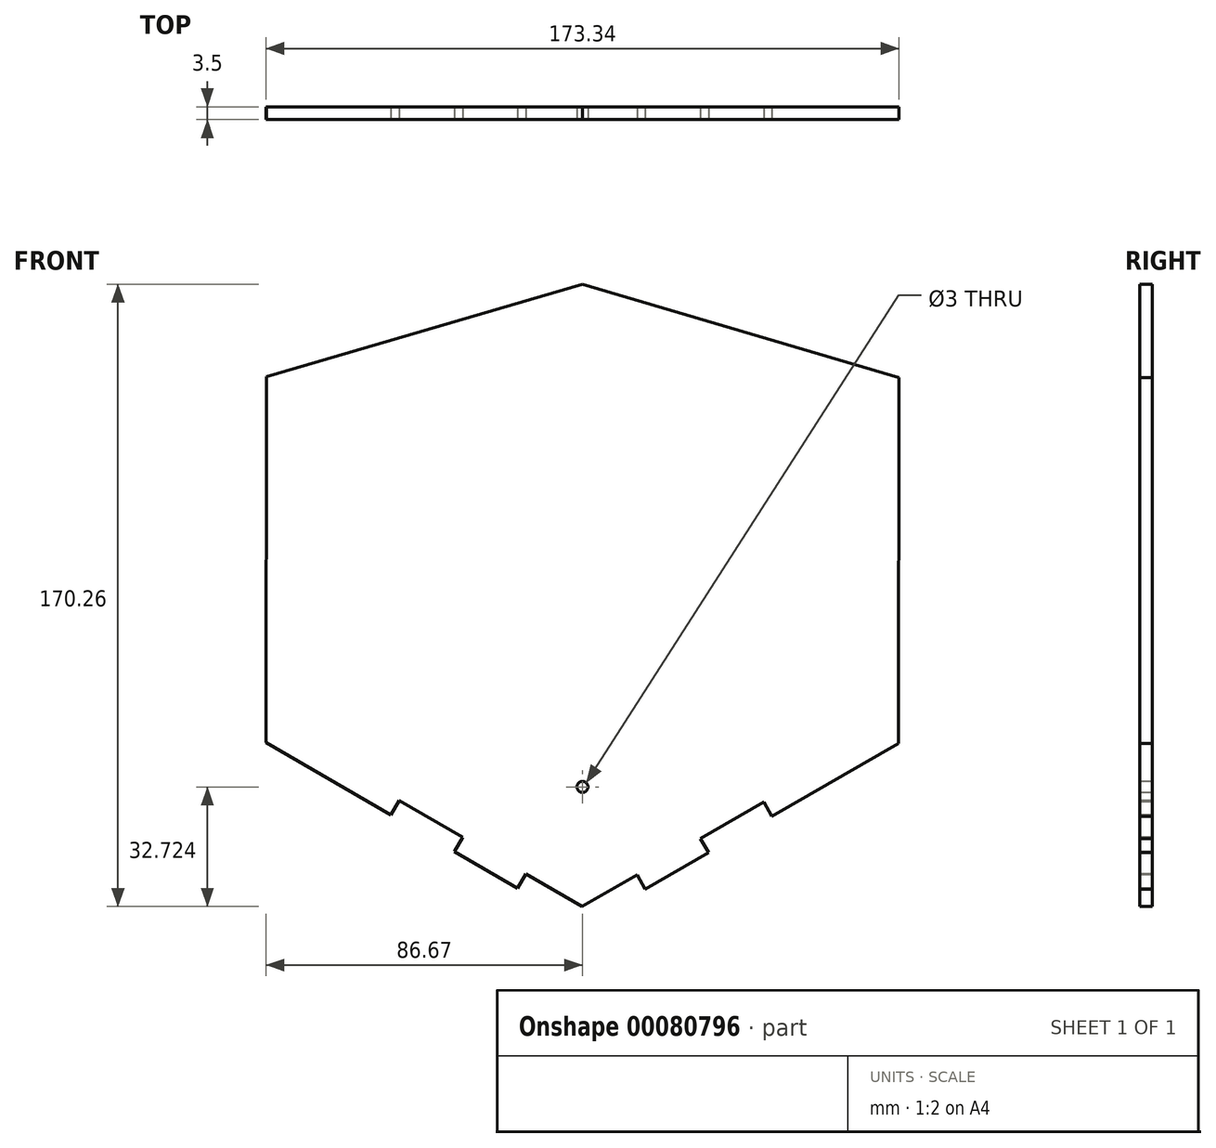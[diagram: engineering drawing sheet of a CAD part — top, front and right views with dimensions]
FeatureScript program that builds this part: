
annotation { "Feature Type Name" : "Feature", "Feature Type Description" : "" }
export const myFeature = defineFeature(function(context is Context, id is Id, definition is map)
    precondition{}
    {
        {
            var Q0;
            Q0=qCreatedBy(makeId("Front.planeOp"),FACE);
            var sketch = newSketch(context, id + "F0", { "sketchPlane" : qUnion([Q0])});
            skCircle(sketch, "E0.cCircle", {"center": v(0, 0) * mm, "radius": 86.6 * mm, "construction": true});
            skLineSegment(sketch, "E0.0", {"start": v(-86.54, 50.12) * mm, "end": v(0.13, 100) * mm});
            skLineSegment(sketch, "E0.1", {"start": v(0.13, 100) * mm, "end": v(86.67, 49.88) * mm});
            skLineSegment(sketch, "E0.2", {"start": v(86.67, 49.88) * mm, "end": v(86.54, -50.12) * mm});
            skLineSegment(sketch, "E0.3", {"start": v(86.54, -50.12) * mm, "end": v(-0.13, -100) * mm});
            skLineSegment(sketch, "E0.4", {"start": v(-0.13, -100) * mm, "end": v(-86.67, -49.88) * mm});
            skLineSegment(sketch, "E0.5", {"start": v(-86.67, -49.88) * mm, "end": v(-86.54, 50.12) * mm});
            skPoint(sketch, "E0.0.midPoint", {"position": v(-43.2, 75.06) * mm});
            skLineSegment(sketch, "E1", {"start": v(-86.54, 50.12) * mm, "end": v(0, 75.46) * mm});
            skLineSegment(sketch, "E2", {"start": v(0, 75.46) * mm, "end": v(86.67, 49.88) * mm});
            skSolve(sketch);
        }
        {
            var Q0;
            Q0=makeQuery(id+"F0.imprint","IMPRINT",FACE,{"disambiguationData":[TD([[makeQuery(id+"F0.imprint","IMPRINT",EDGE,{"derivedFrom":sQuery(id+"F0.wireOp",EDGE,"E0.2")}),-1.0]])]});
            extrude(context, id + "F1", {"entities" : qUnion([Q0]), "depth" : 3.5 * mm});
        }
        {
            var Q0;
            Q0=makeQuery(id+"F1.opExtrude","CAP_FACE",FACE,{"disambiguationData":[OSD([sQuery(id+"F0.wireOp",EDGE,"E0.0"),sQuery(id+"F0.wireOp",EDGE,"E0.1"),sQuery(id+"F0.wireOp",EDGE,"E0.2"),sQuery(id+"F0.wireOp",EDGE,"E0.3"),sQuery(id+"F0.wireOp",EDGE,"E0.4"),sQuery(id+"F0.wireOp",EDGE,"E0.5")])],"isStart":false});
            var sketch = newSketch(context, id + "F2", { "sketchPlane" : qUnion([Q0])});
            skLineSegment(sketch, "E3", {"start": v(-66.96, 56.2) * mm, "end": v(-69.2, 60.1) * mm});
            skLineSegment(sketch, "E4", {"start": v(-69.2, 60.1) * mm, "end": v(-51.87, 70.07) * mm});
            skLineSegment(sketch, "E5", {"start": v(-51.87, 70.07) * mm, "end": v(-49.62, 66.17) * mm});
            skLineSegment(sketch, "E6", {"start": v(-49.62, 66.17) * mm, "end": v(-32.29, 76.15) * mm});
            skLineSegment(sketch, "E7", {"start": v(-32.29, 76.15) * mm, "end": v(-34.53, 80.05) * mm});
            skLineSegment(sketch, "E8", {"start": v(-34.53, 80.05) * mm, "end": v(-17.2, 90.02) * mm});
            skLineSegment(sketch, "E9", {"start": v(-17.2, 90.02) * mm, "end": v(-17.2, 90.02) * mm});
            skLineSegment(sketch, "E10", {"start": v(-17.2, 90.02) * mm, "end": v(0.13, 100) * mm});
            skLineSegment(sketch, "E11", {"start": v(0.13, 100) * mm, "end": v(2.38, 96.1) * mm});
            skLineSegment(sketch, "E12", {"start": v(-17.2, 90.02) * mm, "end": v(-14.95, 86.12) * mm});
            skLineSegment(sketch, "E13", {"start": v(-14.95, 86.12) * mm, "end": v(2.38, 96.1) * mm});
            skLineSegment(sketch, "E14", {"start": v(-86.67, -49.88) * mm, "end": v(-82.14, -49.89) * mm});
            skLineSegment(sketch, "E15", {"start": v(-86.67, -49.88) * mm, "end": v(-86.67, -49.88) * mm});
            skLineSegment(sketch, "E16", {"start": v(-86.54, 50.11) * mm, "end": v(-86.54, 50.12) * mm});
            skLineSegment(sketch, "E17", {"start": v(86.54, -50.12) * mm, "end": v(82.06, -50.11) * mm});
            skLineSegment(sketch, "E18", {"start": v(86.67, 49.88) * mm, "end": v(86.67, 49.89) * mm});
            skLineSegment(sketch, "E19", {"start": v(86.54, -50.12) * mm, "end": v(86.54, -50.12) * mm});
            skLineSegment(sketch, "E20", {"start": v(43.43, 74.93) * mm, "end": v(0.13, 100) * mm});
            skLineSegment(sketch, "E21", {"start": v(67.1, 56.01) * mm, "end": v(69.36, 59.9) * mm});
            skLineSegment(sketch, "E22", {"start": v(69.36, 59.9) * mm, "end": v(52.05, 69.93) * mm});
            skLineSegment(sketch, "E23", {"start": v(52.05, 69.93) * mm, "end": v(49.8, 66.04) * mm});
            skLineSegment(sketch, "E24", {"start": v(49.8, 66.04) * mm, "end": v(32.5, 76.06) * mm});
            skLineSegment(sketch, "E25", {"start": v(32.5, 76.06) * mm, "end": v(34.75, 79.95) * mm});
            skLineSegment(sketch, "E26", {"start": v(34.75, 79.95) * mm, "end": v(17.44, 89.98) * mm});
            skLineSegment(sketch, "E27", {"start": v(17.44, 89.98) * mm, "end": v(15.18, 86.08) * mm});
            skLineSegment(sketch, "E28", {"start": v(15.18, 86.08) * mm, "end": v(-2.12, 96.1) * mm});
            skLineSegment(sketch, "E29", {"start": v(-2.12, 96.1) * mm, "end": v(0.13, 100) * mm});
            skLineSegment(sketch, "E30", {"start": v(-86.67, -49.88) * mm, "end": v(-84.41, -45.99) * mm});
            skLineSegment(sketch, "E31", {"start": v(-84.41, -45.99) * mm, "end": v(-67.1, -56.01) * mm});
            skLineSegment(sketch, "E32", {"start": v(-67.1, -56.01) * mm, "end": v(-69.7, -59.7) * mm});
            skLineSegment(sketch, "E33", {"start": v(-69.7, -59.7) * mm, "end": v(-52.4, -69.73) * mm});
            skLineSegment(sketch, "E34", {"start": v(-52.4, -69.73) * mm, "end": v(-50.13, -65.83) * mm});
            skLineSegment(sketch, "E35", {"start": v(-50.13, -65.83) * mm, "end": v(-32.83, -75.86) * mm});
            skLineSegment(sketch, "E36", {"start": v(-32.83, -75.86) * mm, "end": v(-35.09, -79.76) * mm});
            skLineSegment(sketch, "E37", {"start": v(-35.09, -79.76) * mm, "end": v(-17.78, -89.78) * mm});
            skLineSegment(sketch, "E38", {"start": v(-17.78, -89.78) * mm, "end": v(-15.52, -85.89) * mm});
            skLineSegment(sketch, "E39", {"start": v(-15.52, -85.89) * mm, "end": v(1.78, -95.91) * mm});
            skLineSegment(sketch, "E40", {"start": v(1.78, -95.91) * mm, "end": v(-0.47, -99.8) * mm});
            skLineSegment(sketch, "E41", {"start": v(-0.47, -99.8) * mm, "end": v(-0.13, -100) * mm});
            skLineSegment(sketch, "E42", {"start": v(-0.13, -100) * mm, "end": v(-2.38, -96.1) * mm});
            skLineSegment(sketch, "E43", {"start": v(-2.38, -96.1) * mm, "end": v(14.95, -86.12) * mm});
            skLineSegment(sketch, "E44", {"start": v(14.95, -86.12) * mm, "end": v(17.2, -90.02) * mm});
            skLineSegment(sketch, "E45", {"start": v(17.2, -90.02) * mm, "end": v(34.53, -80.05) * mm});
            skLineSegment(sketch, "E46", {"start": v(34.53, -80.05) * mm, "end": v(32.29, -76.15) * mm});
            skLineSegment(sketch, "E47", {"start": v(32.29, -76.15) * mm, "end": v(49.62, -66.17) * mm});
            skLineSegment(sketch, "E48", {"start": v(49.62, -66.17) * mm, "end": v(51.87, -70.07) * mm});
            skLineSegment(sketch, "E49", {"start": v(52.12, -69.93) * mm, "end": v(69.45, -59.95) * mm});
            skLineSegment(sketch, "E50", {"start": v(69.45, -59.95) * mm, "end": v(67.2, -56.05) * mm});
            skLineSegment(sketch, "E51", {"start": v(67.2, -56.05) * mm, "end": v(84.54, -46.07) * mm});
            skLineSegment(sketch, "E52", {"start": v(84.54, -46.07) * mm, "end": v(86.78, -49.97) * mm});
            skCircle(sketch, "E53", {"center": v(0, -62.08) * mm, "radius": 1.5 * mm});
            skSolve(sketch);
        }
        {
            var Q0;
            Q0=makeQuery(id+"F2.imprint","IMPRINT",FACE,{"disambiguationData":[TD([[makeQuery(id+"F2.imprint","IMPRINT",EDGE,{"derivedFrom":sQuery(id+"F2.wireOp",EDGE,"C7dvouTY-Bt3v-uct5-AHeq-p9BstwpN72ip.bottom")}),-1.0]])]});
            var Q1;
            Q1=makeQuery(id+"F2.imprint","IMPRINT",FACE,{"disambiguationData":[TD([[makeQuery(id+"F2.imprint","IMPRINT",EDGE,{"derivedFrom":sQuery(id+"F2.wireOp",EDGE,"167fa7a6-6e49-4368-af60-a64b96dbe5f00.MirrorCS")}),1.0]])]});
            var Q2;
            {var subQ0=sQuery(id+"F2.wireOp",EDGE,"E21");Q2=makeQuery(id+"F2.imprint","IMPRINT",FACE,{"disambiguationData":[TD([[makeQuery(id+"F2.imprint","IMPRINT",EDGE,{"derivedFrom":subQ0}),-1.0]])]});}
            var Q3;
            {var subQ7=sQuery(id+"F2.wireOp",EDGE,"MmeorMg7-Et77-mlVq-baLl-yIuDlze3Zn6h");Q3=makeQuery(id+"F2.imprint","IMPRINT",FACE,{"disambiguationData":[TD([[makeQuery(id+"F2.imprint","IMPRINT",EDGE,{"derivedFrom":subQ7}),-1.0]])]});}
            var Q4;
            {var subQ0=sQuery(id+"F2.wireOp",EDGE,"Vk6HYr1c-dtAy-F9Vo-Em9N-zrXxlWtmeyFl");Q4=makeQuery(id+"F2.imprint","IMPRINT",FACE,{"disambiguationData":[TD([[makeQuery(id+"F2.imprint","IMPRINT",EDGE,{"derivedFrom":subQ0}),-1.0]])]});}
            var Q5;
            {var subQ4=sQuery(id+"F2.wireOp",EDGE,"E17");Q5=makeQuery(id+"F2.imprint","IMPRINT",FACE,{"disambiguationData":[TD([[makeQuery(id+"F2.imprint","IMPRINT",EDGE,{"derivedFrom":subQ4}),1.0]])]});}
            var Q6;
            {var subQ7=sQuery(id+"F2.wireOp",EDGE,"2hepQ55R-wE0u-Nrot-sNKX-UqjB5rhPEbW4");Q6=makeQuery(id+"F2.imprint","IMPRINT",FACE,{"disambiguationData":[TD([[makeQuery(id+"F2.imprint","IMPRINT",EDGE,{"derivedFrom":subQ7}),-1.0]])]});}
            var Q7;
            {var subQ0=sQuery(id+"F2.wireOp",EDGE,"E46");Q7=makeQuery(id+"F2.imprint","IMPRINT",FACE,{"disambiguationData":[TD([[makeQuery(id+"F2.imprint","IMPRINT",EDGE,{"derivedFrom":subQ0}),-1.0]])]});}
            var Q8;
            {var subQ8=sQuery(id+"F2.wireOp",EDGE,"E38");Q8=makeQuery(id+"F2.imprint","IMPRINT",FACE,{"disambiguationData":[TD([[makeQuery(id+"F2.imprint","IMPRINT",EDGE,{"derivedFrom":subQ8}),-1.0]])]});}
            var Q9;
            {var subQ2=sQuery(id+"F2.wireOp",EDGE,"E14");Q9=makeQuery(id+"F2.imprint","IMPRINT",FACE,{"disambiguationData":[TD([[makeQuery(id+"F2.imprint","IMPRINT",EDGE,{"derivedFrom":subQ2}),-1.0]])]});}
            var Q10;
            {var subQ4=sQuery(id+"F2.wireOp",EDGE,"0MOvUSSM-JEJ4-uT5y-fSHd-BTDzLtKJbzvy");Q10=makeQuery(id+"F2.imprint","IMPRINT",FACE,{"disambiguationData":[TD([[makeQuery(id+"F2.imprint","IMPRINT",EDGE,{"derivedFrom":subQ4}),1.0]])]});}
            var Q11;
            {var subQ1=sQuery(id+"F2.wireOp",EDGE,"TpYNR21e-QnRL-vsfI-uHCN-WWDlJ3sKFpeB");Q11=makeQuery(id+"F2.imprint","IMPRINT",FACE,{"disambiguationData":[TD([[makeQuery(id+"F2.imprint","IMPRINT",EDGE,{"derivedFrom":subQ1}),-1.0]])]});}
            var Q12;
            {var subQ0=sQuery(id+"F2.wireOp",EDGE,"UFPksVoi-JG3M-WY3m-71ca-0zyNUTbbqVwQ");Q12=makeQuery(id+"F2.imprint","IMPRINT",FACE,{"disambiguationData":[TD([[makeQuery(id+"F2.imprint","IMPRINT",EDGE,{"derivedFrom":subQ0}),-1.0]])]});}
            var Q13;
            {var subQ5=sQuery(id+"F2.wireOp",EDGE,"E3");Q13=makeQuery(id+"F2.imprint","IMPRINT",FACE,{"disambiguationData":[TD([[makeQuery(id+"F2.imprint","IMPRINT",EDGE,{"derivedFrom":subQ5}),1.0]])]});}
            var Q14;
            {var subQ0=sQuery(id+"F2.wireOp",EDGE,"E5");Q14=makeQuery(id+"F2.imprint","IMPRINT",FACE,{"disambiguationData":[TD([[makeQuery(id+"F2.imprint","IMPRINT",EDGE,{"derivedFrom":subQ0}),1.0]])]});}
            var Q15;
            Q15=makeQuery(id+"F2.imprint","IMPRINT",FACE,{"disambiguationData":[TD([[makeQuery(id+"F2.imprint","IMPRINT",EDGE,{"derivedFrom":sQuery(id+"F2.wireOp",EDGE,"E10")}),-1.0]])]});
            var Q16;
            {var subQ2=sQuery(id+"F2.wireOp",EDGE,"E11");Q16=makeQuery(id+"F2.imprint","IMPRINT",FACE,{"disambiguationData":[TD([[makeQuery(id+"F2.imprint","IMPRINT",EDGE,{"derivedFrom":subQ2}),1.0]])]});}
            var Q17;
            {var subQ1=sQuery(id+"F2.wireOp",EDGE,"E23");Q17=makeQuery(id+"F2.imprint","IMPRINT",FACE,{"disambiguationData":[TD([[makeQuery(id+"F2.imprint","IMPRINT",EDGE,{"derivedFrom":subQ1}),-1.0]])]});}
            var Q18;
            {var subQ0=sQuery(id+"F2.wireOp",EDGE,"E34");Q18=makeQuery(id+"F2.imprint","IMPRINT",FACE,{"disambiguationData":[TD([[makeQuery(id+"F2.imprint","IMPRINT",EDGE,{"derivedFrom":subQ0}),-1.0]])]});}
            var Q19;
            {var subQ0=sQuery(id+"F2.wireOp",EDGE,"E14");Q19=makeQuery(id+"F2.imprint","IMPRINT",FACE,{"disambiguationData":[TD([[makeQuery(id+"F2.imprint","IMPRINT",EDGE,{"derivedFrom":subQ0}),1.0]])]});}
            var Q20;
            {var subQ0=sQuery(id+"F2.wireOp",EDGE,"cuXqOJ30-Zwg1-tR57-076Y-P6XMJI0WWfx9");var subQ1=sQuery(id+"F2.wireOp",EDGE,"5aIRCDt4-DOAl-4ROM-u9rs-yZQl9E3yMdo4");var subQ2=makeQuery(id+"F2.imprint","INTERSECT",VERTEX,{"derivedFrom":[subQ1,subQ0]});Q20=makeQuery(id+"F2.imprint","IMPRINT",FACE,{"disambiguationData":[TD([[makeQuery(id+"F2.imprint","IMPRINT",EDGE,{"disambiguationData":[TD([[subQ2,1.0]])],"derivedFrom":subQ1}),1.0]])]});}
            var Q21;
            {var subQ0=sQuery(id+"F2.wireOp",EDGE,"E11");Q21=makeQuery(id+"F2.imprint","IMPRINT",FACE,{"disambiguationData":[TD([[makeQuery(id+"F2.imprint","IMPRINT",EDGE,{"derivedFrom":subQ0}),-1.0]])]});}
            var Q22;
            {var subQ3=sQuery(id+"F2.wireOp",EDGE,"6yJ81mIp-N93a-gt9v-nsp0-4odaCLWb8l0v");var subQ5=sQuery(id+"F2.wireOp",EDGE,"VxHAfr01-ARXi-U8Iy-wC3h-sixUrLqSzS5g");var subQ9=makeQuery(id+"F2.imprint","INTERSECT",VERTEX,{"derivedFrom":[subQ3,subQ5]});Q22=makeQuery(id+"F2.imprint","IMPRINT",FACE,{"disambiguationData":[TD([[makeQuery(id+"F2.imprint","IMPRINT",EDGE,{"disambiguationData":[TD([[subQ9,1.0]])],"derivedFrom":subQ3}),-1.0]])]});}
            var Q23;
            {var subQ7=sQuery(id+"F2.wireOp",EDGE,"E17");Q23=makeQuery(id+"F2.imprint","IMPRINT",FACE,{"disambiguationData":[TD([[makeQuery(id+"F2.imprint","IMPRINT",EDGE,{"derivedFrom":subQ7}),-1.0]])]});}
            var Q24;
            {var subQ0=sQuery(id+"F2.wireOp",EDGE,"E40");var subQ1=sQuery(id+"F2.wireOp",EDGE,"E39");var subQ2=makeQuery(id+"F2.imprint","INTERSECT",VERTEX,{"derivedFrom":[subQ1,subQ0]});Q24=makeQuery(id+"F2.imprint","IMPRINT",FACE,{"disambiguationData":[TD([[makeQuery(id+"F2.imprint","IMPRINT",EDGE,{"disambiguationData":[TD([[subQ2,1.0]])],"derivedFrom":subQ1}),-1.0]])]});}
            var Q25;
            {var subQ0=sQuery(id+"F2.wireOp",EDGE,"E44");Q25=makeQuery(id+"F2.imprint","IMPRINT",FACE,{"disambiguationData":[TD([[makeQuery(id+"F2.imprint","IMPRINT",EDGE,{"derivedFrom":subQ0}),-1.0]])]});}
            var Q26;
            {var subQ0=sQuery(id+"F2.wireOp",EDGE,"E41");Q26=makeQuery(id+"F2.imprint","IMPRINT",FACE,{"disambiguationData":[TD([[makeQuery(id+"F2.imprint","IMPRINT",EDGE,{"derivedFrom":subQ0}),-1.0]])]});}
            var Q27;
            Q27=makeQuery(id+"F2.imprint","IMPRINT",FACE,{"disambiguationData":[TD([[makeQuery(id+"F2.imprint","IMPRINT",EDGE,{"derivedFrom":sQuery(id+"F2.wireOp",EDGE,"E53")}),1.0]])]});
            extrude(context, id + "F3", {"entities" : qUnion([Q0, Q1, Q2, Q3, Q4, Q5, Q6, Q7, Q8, Q9, Q10, Q11, Q12, Q13, Q14, Q15, Q16, Q17, Q18, Q19, Q20, Q21, Q22, Q23, Q24, Q25, Q26, Q27]), "operationType" : NewBodyOperationType.REMOVE, "oppositeDirection" : true, "depth" : 25 * mm});
        }
    });
